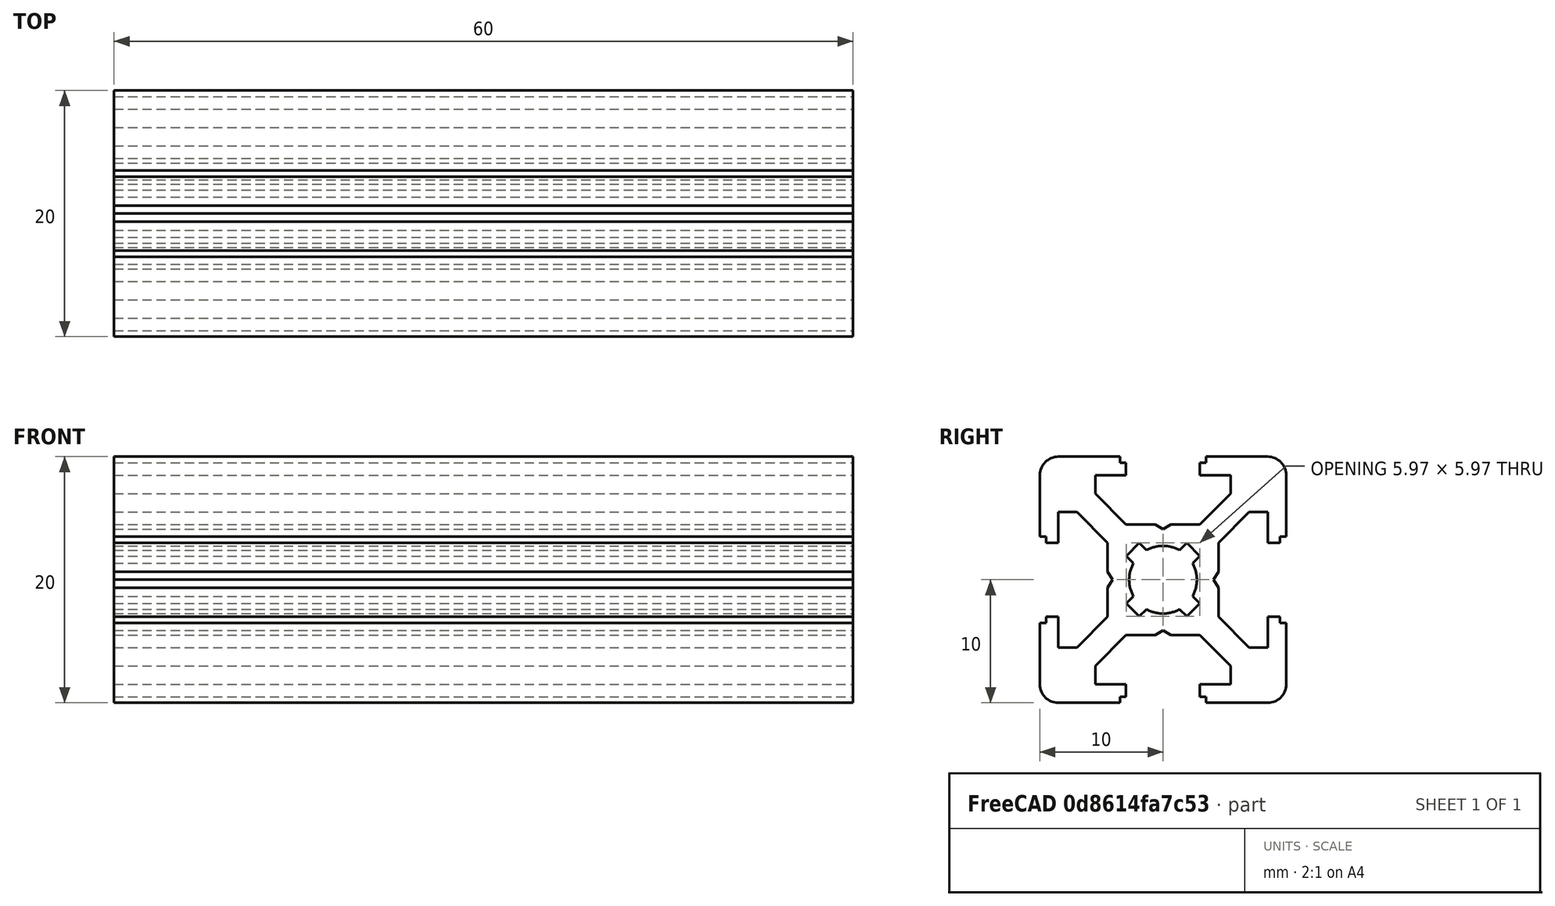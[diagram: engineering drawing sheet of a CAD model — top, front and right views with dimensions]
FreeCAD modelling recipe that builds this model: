
FCSTD DOCUMENT  (FreeCAD 0.19R)
Label: Tslot6
License: All rights reserved
LicenseURL: http://en.wikipedia.org/wiki/All_rights_reserved
objects: Sketcher::SketchObject×1, PartDesign::Pad×1, PartDesign::Body×1
note: 4 computed .brp shape members not serialized (recipe doc carries the construction recipe); baked Part::Feature solids carry a one-line shape summary decoded from their .brp

FEATURE [Sketcher::SketchObject] Sketch  label="T-Slot-Skizze"
  FullyConstrained = true
  MapMode = 5
  Placement = pos=(0,0,0) rot=(0.57735,0.57735,0.57735;2.0944rad)
  Support = -> [YZ_Plane]
  sketch-geometry (98):
    g0: LineSegment StartX=0 StartY=4.1 StartZ=0 EndX=0.65 EndY=4.5 EndZ=0
    g1: LineSegment StartX=0.65 StartY=4.5 StartZ=0 EndX=3 EndY=4.5 EndZ=0
    g2: LineSegment StartX=3 StartY=4.5 StartZ=0 EndX=5.5 EndY=7 EndZ=0
    g3: LineSegment StartX=5.5 StartY=7 StartZ=0 EndX=5.5 EndY=8.5 EndZ=0
    g4: LineSegment StartX=5.5 StartY=8.5 StartZ=0 EndX=3 EndY=8.5 EndZ=0
    g5: LineSegment StartX=3 StartY=8.5 StartZ=0 EndX=3 EndY=9.5 EndZ=0
    g6: LineSegment StartX=3 StartY=9.5 StartZ=0 EndX=3.5 EndY=9.5 EndZ=0
    g7: LineSegment StartX=3.5 StartY=9.5 StartZ=0 EndX=3.5 EndY=10 EndZ=0
    g8: LineSegment StartX=3.5 StartY=10 StartZ=0 EndX=8.5 EndY=10 EndZ=0
    g9: LineSegment StartX=10 StartY=8.5 StartZ=0 EndX=10 EndY=3.5 EndZ=0
    g10: LineSegment StartX=10 StartY=3.5 StartZ=0 EndX=9.5 EndY=3.5 EndZ=0
    g11: LineSegment StartX=9.5 StartY=3.5 StartZ=0 EndX=9.5 EndY=3 EndZ=0
    g12: LineSegment StartX=9.5 StartY=3 StartZ=0 EndX=8.5 EndY=3 EndZ=0
    g13: LineSegment StartX=8.5 StartY=3 StartZ=0 EndX=8.5 EndY=5.5 EndZ=0
    g14: LineSegment StartX=8.5 StartY=5.5 StartZ=0 EndX=7 EndY=5.5 EndZ=0
    g15: LineSegment StartX=7 StartY=5.5 StartZ=0 EndX=4.5 EndY=3 EndZ=0
    g16: LineSegment StartX=4.5 StartY=3 StartZ=0 EndX=4.5 EndY=0.65 EndZ=0
    g17: LineSegment StartX=4.5 StartY=0.65 StartZ=0 EndX=4.1 EndY=0 EndZ=0
    g18: ArcOfCircle CenterX=8.5 CenterY=8.5 CenterZ=0 NormalX=0 NormalY=0 NormalZ=1 AngleXU=0 Radius=1.5 StartAngle=0 EndAngle=1.5708
    g19: LineSegment StartX=0 StartY=-4.1 StartZ=0 EndX=0.65 EndY=-4.5 EndZ=0
    g20: LineSegment StartX=0.65 StartY=-4.5 StartZ=0 EndX=3 EndY=-4.5 EndZ=0
    g21: LineSegment StartX=3 StartY=-4.5 StartZ=0 EndX=5.5 EndY=-7 EndZ=0
    g22: LineSegment StartX=5.5 StartY=-7 StartZ=0 EndX=5.5 EndY=-8.5 EndZ=0
    g23: LineSegment StartX=5.5 StartY=-8.5 StartZ=0 EndX=3 EndY=-8.5 EndZ=0
    g24: LineSegment StartX=3 StartY=-8.5 StartZ=0 EndX=3 EndY=-9.5 EndZ=0
    g25: LineSegment StartX=3 StartY=-9.5 StartZ=0 EndX=3.5 EndY=-9.5 EndZ=0
    g26: LineSegment StartX=3.5 StartY=-9.5 StartZ=0 EndX=3.5 EndY=-10 EndZ=0
    g27: LineSegment StartX=3.5 StartY=-10 StartZ=0 EndX=8.5 EndY=-10 EndZ=0
    g28: LineSegment StartX=10 StartY=-8.5 StartZ=0 EndX=10 EndY=-3.5 EndZ=0
    g29: LineSegment StartX=10 StartY=-3.5 StartZ=0 EndX=9.5 EndY=-3.5 EndZ=0
    g30: LineSegment StartX=9.5 StartY=-3.5 StartZ=0 EndX=9.5 EndY=-3 EndZ=0
    g31: LineSegment StartX=9.5 StartY=-3 StartZ=0 EndX=8.5 EndY=-3 EndZ=0
    g32: LineSegment StartX=8.5 StartY=-3 StartZ=0 EndX=8.5 EndY=-5.5 EndZ=0
    g33: LineSegment StartX=8.5 StartY=-5.5 StartZ=0 EndX=7 EndY=-5.5 EndZ=0
    g34: LineSegment StartX=7 StartY=-5.5 StartZ=0 EndX=4.5 EndY=-3 EndZ=0
    g35: LineSegment StartX=4.5 StartY=-3 StartZ=0 EndX=4.5 EndY=-0.65 EndZ=0
    g36: ArcOfCircle CenterX=8.5 CenterY=-8.5 CenterZ=0 NormalX=0 NormalY=0 NormalZ=1 AngleXU=0 Radius=1.5 StartAngle=4.71239 EndAngle=6.28319
    g37: LineSegment StartX=4.5 StartY=-0.65 StartZ=0 EndX=4.1 EndY=0 EndZ=0
    g38: LineSegment StartX=0 StartY=-4.1 StartZ=0 EndX=-0.65 EndY=-4.5 EndZ=0
    g39: LineSegment StartX=-0.65 StartY=-4.5 StartZ=0 EndX=-3 EndY=-4.5 EndZ=0
    g40: LineSegment StartX=-3 StartY=-4.5 StartZ=0 EndX=-5.5 EndY=-7 EndZ=0
    g41: LineSegment StartX=-5.5 StartY=-7 StartZ=0 EndX=-5.5 EndY=-8.5 EndZ=0
    g42: LineSegment StartX=-5.5 StartY=-8.5 StartZ=0 EndX=-3 EndY=-8.5 EndZ=0
    g43: LineSegment StartX=-3 StartY=-8.5 StartZ=0 EndX=-3 EndY=-9.5 EndZ=0
    g44: LineSegment StartX=-3 StartY=-9.5 StartZ=0 EndX=-3.5 EndY=-9.5 EndZ=0
    g45: LineSegment StartX=-3.5 StartY=-9.5 StartZ=0 EndX=-3.5 EndY=-10 EndZ=0
    g46: LineSegment StartX=-3.5 StartY=-10 StartZ=0 EndX=-8.5 EndY=-10 EndZ=0
    g47: LineSegment StartX=-10 StartY=-8.5 StartZ=0 EndX=-10 EndY=-3.5 EndZ=0
    g48: LineSegment StartX=-10 StartY=-3.5 StartZ=0 EndX=-9.5 EndY=-3.5 EndZ=0
    g49: LineSegment StartX=-9.5 StartY=-3.5 StartZ=0 EndX=-9.5 EndY=-3 EndZ=0
    g50: LineSegment StartX=-9.5 StartY=-3 StartZ=0 EndX=-8.5 EndY=-3 EndZ=0
    g51: LineSegment StartX=-8.5 StartY=-3 StartZ=0 EndX=-8.5 EndY=-5.5 EndZ=0
    g52: LineSegment StartX=-8.5 StartY=-5.5 StartZ=0 EndX=-7 EndY=-5.5 EndZ=0
    g53: LineSegment StartX=-7 StartY=-5.5 StartZ=0 EndX=-4.5 EndY=-3 EndZ=0
    g54: LineSegment StartX=-4.5 StartY=-3 StartZ=0 EndX=-4.5 EndY=-0.65 EndZ=0
    g55: ArcOfCircle CenterX=-8.5 CenterY=-8.5 CenterZ=0 NormalX=0 NormalY=0 NormalZ=1 AngleXU=0 Radius=1.5 StartAngle=3.14159 EndAngle=4.71239
    g56: LineSegment StartX=-4.5 StartY=-0.65 StartZ=0 EndX=-4.1 EndY=0 EndZ=0
    g57: LineSegment StartX=-0.65 StartY=4.5 StartZ=0 EndX=-3 EndY=4.5 EndZ=0
    g58: LineSegment StartX=-3 StartY=4.5 StartZ=0 EndX=-5.5 EndY=7 EndZ=0
    g59: LineSegment StartX=-5.5 StartY=7 StartZ=0 EndX=-5.5 EndY=8.5 EndZ=0
    g60: LineSegment StartX=-5.5 StartY=8.5 StartZ=0 EndX=-3 EndY=8.5 EndZ=0
    g61: LineSegment StartX=-3 StartY=8.5 StartZ=0 EndX=-3 EndY=9.5 EndZ=0
    g62: LineSegment StartX=-3 StartY=9.5 StartZ=0 EndX=-3.5 EndY=9.5 EndZ=0
    g63: LineSegment StartX=-3.5 StartY=9.5 StartZ=0 EndX=-3.5 EndY=10 EndZ=0
    g64: LineSegment StartX=-3.5 StartY=10 StartZ=0 EndX=-8.5 EndY=10 EndZ=0
    g65: LineSegment StartX=-10 StartY=8.5 StartZ=0 EndX=-10 EndY=3.5 EndZ=0
    g66: LineSegment StartX=-10 StartY=3.5 StartZ=0 EndX=-9.5 EndY=3.5 EndZ=0
    g67: LineSegment StartX=-9.5 StartY=3.5 StartZ=0 EndX=-9.5 EndY=3 EndZ=0
    g68: LineSegment StartX=-9.5 StartY=3 StartZ=0 EndX=-8.5 EndY=3 EndZ=0
    g69: LineSegment StartX=-8.5 StartY=3 StartZ=0 EndX=-8.5 EndY=5.5 EndZ=0
    g70: LineSegment StartX=-8.5 StartY=5.5 StartZ=0 EndX=-7 EndY=5.5 EndZ=0
    g71: LineSegment StartX=-7 StartY=5.5 StartZ=0 EndX=-4.5 EndY=3 EndZ=0
    g72: LineSegment StartX=-4.5 StartY=3 StartZ=0 EndX=-4.5 EndY=0.65 EndZ=0
    g73: ArcOfCircle CenterX=-8.5 CenterY=8.5 CenterZ=0 NormalX=0 NormalY=0 NormalZ=1 AngleXU=0 Radius=1.5 StartAngle=1.5708 EndAngle=3.14159
    g74: LineSegment StartX=-4.5 StartY=0.65 StartZ=0 EndX=-4.1 EndY=0 EndZ=0
    g75: LineSegment StartX=0 StartY=4.1 StartZ=0 EndX=-0.65 EndY=4.5 EndZ=0
    g76: Circle CenterX=0 CenterY=0 CenterZ=0 NormalX=0 NormalY=0 NormalZ=1 AngleXU=0 Radius=3.55
    g77: Circle CenterX=0 CenterY=0 CenterZ=0 NormalX=0 NormalY=0 NormalZ=1 AngleXU=0 Radius=2.75
    g78: LineSegment StartX=1.3405 StartY=2.40116 StartZ=0 EndX=1.92324 EndY=2.9839 EndZ=0
    g79: LineSegment StartX=1.92324 StartY=2.9839 StartZ=0 EndX=2.9839 EndY=1.92324 EndZ=0
    g80: LineSegment StartX=2.9839 StartY=1.92324 StartZ=0 EndX=2.40116 EndY=1.3405 EndZ=0
    g81: ArcOfCircle CenterX=0 CenterY=0 CenterZ=0 NormalX=0 NormalY=0 NormalZ=1 AngleXU=0 Radius=2.75 StartAngle=0 EndAngle=0.509172
    g82: ArcOfCircle CenterX=0 CenterY=0 CenterZ=0 NormalX=0 NormalY=0 NormalZ=1 AngleXU=0 Radius=2.75 StartAngle=1.06162 EndAngle=1.5708
    g83: LineSegment StartX=-1.3405 StartY=2.40116 StartZ=0 EndX=-1.92324 EndY=2.9839 EndZ=0
    g84: LineSegment StartX=-1.92324 StartY=2.9839 StartZ=0 EndX=-2.9839 EndY=1.92324 EndZ=0
    g85: LineSegment StartX=-2.9839 StartY=1.92324 StartZ=0 EndX=-2.40116 EndY=1.3405 EndZ=0
    g86: ArcOfCircle CenterX=-1.3e-15 CenterY=6e-16 CenterZ=0 NormalX=0 NormalY=0 NormalZ=1 AngleXU=0 Radius=2.75 StartAngle=2.63242 EndAngle=3.14159
    g87: ArcOfCircle CenterX=-1.3e-15 CenterY=6e-16 CenterZ=0 NormalX=0 NormalY=0 NormalZ=1 AngleXU=0 Radius=2.75 StartAngle=1.5708 EndAngle=2.07997
    g88: LineSegment StartX=-1.34051 StartY=-2.40115 StartZ=0 EndX=-1.92325 EndY=-2.98389 EndZ=0
    g89: LineSegment StartX=-1.92325 StartY=-2.98389 StartZ=0 EndX=-2.9839 EndY=-1.92323 EndZ=0
    g90: LineSegment StartX=-2.9839 StartY=-1.92323 StartZ=0 EndX=-2.40116 EndY=-1.34049 EndZ=0
    g91: ArcOfCircle CenterX=-3e-16 CenterY=2e-16 CenterZ=0 NormalX=0 NormalY=0 NormalZ=1 AngleXU=0 Radius=2.75 StartAngle=3.14159 EndAngle=3.65076
    g92: ArcOfCircle CenterX=-3e-16 CenterY=2e-16 CenterZ=0 NormalX=0 NormalY=0 NormalZ=1 AngleXU=0 Radius=2.75 StartAngle=4.20321 EndAngle=4.71239
    g93: LineSegment StartX=1.34051 StartY=-2.40115 StartZ=0 EndX=1.92325 EndY=-2.98389 EndZ=0
    g94: LineSegment StartX=1.92325 StartY=-2.98389 StartZ=0 EndX=2.9839 EndY=-1.92323 EndZ=0
    g95: LineSegment StartX=2.9839 StartY=-1.92323 StartZ=0 EndX=2.40116 EndY=-1.34049 EndZ=0
    g96: ArcOfCircle CenterX=3e-16 CenterY=2e-16 CenterZ=0 NormalX=0 NormalY=0 NormalZ=1 AngleXU=0 Radius=2.75 StartAngle=4.71239 EndAngle=5.22156
    g97: ArcOfCircle CenterX=3e-16 CenterY=2e-16 CenterZ=0 NormalX=0 NormalY=0 NormalZ=1 AngleXU=0 Radius=2.75 StartAngle=5.77402 EndAngle=6.28319
  constraints (291):
    c: PointOnObject(g0,g-2)
    c: Coincident(g0,g1)
    c: Horizontal(g1)
    c: Coincident(g1,g2)
    c: Coincident(g2,g3)
    c: Vertical(g3)
    c: Coincident(g3,g4)
    c: Horizontal(g4)
    c: Coincident(g4,g5)
    c: Vertical(g5)
    c: Coincident(g5,g6)
    c: Horizontal(g6)
    c: Coincident(g6,g7)
    c: Coincident(g7,g8)
    c: Horizontal(g8)
    c: Vertical(g7)
    c: DistanceX(g-1,g5) = 3
    c: DistanceY(g4,g7) = 1.5
    c: DistanceY(g0,g7) = 5.5
    c: DistanceY(g3,g3) = 1.5
    c: DistanceY(g4,g5) = 1
    c: DistanceX(g-1,g1) = 3
    c: DistanceX(g-1,g7) = 3.5
    c: DistanceX(g0,g0) = 0.65
    c: DistanceY(g0,g0) = 0.4
    c: DistanceX(g-1,g3) = 5.5
    c: Vertical(g9)
    c: Coincident(g9,g10)
    c: Coincident(g10,g11)
    c: Coincident(g11,g12)
    c: Coincident(g12,g13)
    c: Vertical(g13)
    c: Coincident(g13,g14)
    c: Horizontal(g14)
    c: Coincident(g14,g15)
    c: Coincident(g15,g16)
    c: Vertical(g16)
    c: Coincident(g16,g17)
    c: PointOnObject(g17,g-1)
    c: Horizontal(g10)
    c: Horizontal(g12)
    c: Vertical(g11)
    c: Equal(g17,g0)
    c: Equal(g1,g16)
    c: Equal(g15,g2)
    c: Equal(g3,g14)
    c: Equal(g13,g4)
    c: Equal(g12,g5)
    c: Parallel(g15,g2)
    c: Equal(g11,g6)
    c: Equal(g10,g7)
    c: Equal(g9,g8)
    c: Tangent(g8,g18) = 1.5708
    c: Tangent(g9,g18) = 1.5708
    c: Radius(g18) = 1.5
    c: DistanceY(g-1,g8) = 10
    c: DistanceX(g-1,g9) = 10
    c: Coincident(g19,g20)
    c: Horizontal(g20)
    c: Coincident(g20,g21)
    c: Coincident(g21,g22)
    c: Vertical(g22)
    c: Coincident(g22,g23)
    c: Horizontal(g23)
    c: Coincident(g23,g24)
    c: Vertical(g24)
    c: Coincident(g24,g25)
    c: Horizontal(g25)
    c: Coincident(g25,g26)
    c: Coincident(g26,g27)
    c: Horizontal(g27)
    c: Vertical(g26)
    c: Vertical(g28)
    c: Coincident(g28,g29)
    c: Coincident(g29,g30)
    c: Coincident(g30,g31)
    c: Coincident(g31,g32)
    c: Vertical(g32)
    c: Coincident(g32,g33)
    c: Horizontal(g33)
    c: Coincident(g33,g34)
    c: Coincident(g34,g35)
    c: Vertical(g35)
    c: Coincident(g35,g37)
    c: Horizontal(g29)
    c: Horizontal(g31)
    c: Vertical(g30)
    c: Equal(g37,g19)
    c: Equal(g20,g35)
    c: Equal(g34,g21)
    c: Equal(g22,g33)
    c: Equal(g32,g23)
    c: Equal(g31,g24)
    c: Parallel(g34,g21)
    c: Equal(g30,g25)
    c: Equal(g29,g26)
    c: Equal(g28,g27)
    c: Tangent(g27,g36) = -1.5708
    c: Tangent(g28,g36) = -1.5708
    c: Radius(g36) = 1.5
    c: Equal(g9,g28)
    c: Equal(g12,g31)
    c: DistanceX(g-1,g28) = 10
    c: DistanceY(g27,g-1) = 10
    c: DistanceY(g30,g-1) = 3
    c: Equal(g33,g14)
    c: Equal(g35,g16)
    c: Equal(g17,g37)
    c: Coincident(g37,g17)
    c: Equal(g15,g34)
    c: PointOnObject(g19,g-2)
    c: DistanceY(g34,g-1) = 3
    c: DistanceX(g-1,g20) = 3
    c: Coincident(g38,g39)
    c: Horizontal(g39)
    c: Coincident(g39,g40)
    c: Coincident(g40,g41)
    c: Vertical(g41)
    c: Coincident(g41,g42)
    c: Horizontal(g42)
    c: Coincident(g42,g43)
    c: Vertical(g43)
    c: Coincident(g43,g44)
    c: Horizontal(g44)
    c: Coincident(g44,g45)
    c: Coincident(g45,g46)
    c: Horizontal(g46)
    c: Vertical(g45)
    c: Vertical(g47)
    c: Coincident(g47,g48)
    c: Coincident(g48,g49)
    c: Coincident(g49,g50)
    c: Coincident(g50,g51)
    c: Vertical(g51)
    c: Coincident(g51,g52)
    c: Horizontal(g52)
    c: Coincident(g52,g53)
    c: Coincident(g53,g54)
    c: Vertical(g54)
    c: Coincident(g54,g56)
    c: Horizontal(g48)
    c: Horizontal(g50)
    c: Vertical(g49)
    c: Equal(g39,g54)
    c: Equal(g53,g40)
    c: Equal(g41,g52)
    c: Equal(g51,g42)
    c: Equal(g50,g43)
    c: Parallel(g53,g40)
    c: Equal(g49,g44)
    c: Equal(g48,g45)
    c: Equal(g47,g46)
    c: Tangent(g46,g55) = 1.5708
    c: Tangent(g47,g55) = 1.5708
    c: Radius(g55) = 1.5
    c: Coincident(g38,g19)
    c: DistanceX(g39,g-1) = 3
    c: DistanceX(g38,g19) = 0.65
    c: DistanceY(g38,g19) = 0.4
    c: PointOnObject(g56,g-1)
    c: Equal(g56,g38)
    c: DistanceY(g53,g-1) = 3
    c: Equal(g22,g41)
    c: Equal(g42,g23)
    c: Equal(g24,g43)
    c: Equal(g25,g44)
    c: Equal(g26,g45)
    c: DistanceY(g46,g-1) = 10
    c: DistanceX(g47,g-1) = 10
    c: Coincident(g75,g57)
    c: Horizontal(g57)
    c: Coincident(g57,g58)
    c: Coincident(g58,g59)
    c: Vertical(g59)
    c: Coincident(g59,g60)
    c: Horizontal(g60)
    c: Coincident(g60,g61)
    c: Vertical(g61)
    c: Coincident(g61,g62)
    c: Horizontal(g62)
    c: Coincident(g62,g63)
    c: Coincident(g63,g64)
    c: Horizontal(g64)
    c: Vertical(g63)
    c: Vertical(g65)
    c: Coincident(g65,g66)
    c: Coincident(g66,g67)
    c: Coincident(g67,g68)
    c: Coincident(g68,g69)
    c: Vertical(g69)
    c: Coincident(g69,g70)
    c: Horizontal(g70)
    c: Coincident(g70,g71)
    c: Coincident(g71,g72)
    c: Vertical(g72)
    c: Coincident(g72,g74)
    c: Horizontal(g66)
    c: Horizontal(g68)
    c: Vertical(g67)
    c: Equal(g57,g72)
    c: Equal(g71,g58)
    c: Equal(g59,g70)
    c: Equal(g69,g60)
    c: Equal(g68,g61)
    c: Parallel(g71,g58)
    c: Equal(g67,g62)
    c: Equal(g66,g63)
    c: Equal(g65,g64)
    c: Tangent(g64,g73) = -1.5708
    c: Tangent(g65,g73) = -1.5708
    c: Radius(g73) = 1.5
    c: Equal(g74,g75)
    c: Coincident(g56,g74)
    c: Coincident(g0,g75)
    c: Equal(g0,g75)
    c: Equal(g1,g57)
    c: Equal(g2,g58)
    c: Equal(g3,g59)
    c: Equal(g4,g60)
    c: Equal(g5,g61)
    c: Equal(g6,g62)
    c: Equal(g7,g63)
    c: Equal(g8,g64)
    c: DistanceX(g65,g-1) = 10
    c: Coincident(g76,g-1)
    c: Coincident(g77,g-1)
    c: Radius(g76) = 3.55
    c: Radius(g77) = 2.75
    c: PointOnObject(g78,g77)
    c: PointOnObject(g78,g76)
    c: Coincident(g78,g79)
    c: PointOnObject(g79,g76)
    c: Coincident(g79,g80)
    c: PointOnObject(g80,g77)
    c: Coincident(g81,g-1)
    c: Coincident(g81,g80)
    c: Coincident(g82,g81)
    c: Coincident(g82,g78)
    c: Parallel(g78,g80)
    c: Parallel(g78,g2)
    c: Distance(g79) = 1.5
    c: Distance(g78,g80) = 1.5
    c: PointOnObject(g82,g-2)
    c: PointOnObject(g81,g-1)
    c: Coincident(g83,g84)
    c: Coincident(g84,g85)
    c: Coincident(g86,g85)
    c: Coincident(g87,g86)
    c: Coincident(g87,g83)
    c: Parallel(g83,g85)
    c: Distance(g84) = 1.5
    c: Distance(g83,g85) = 1.5
    c: Coincident(g82,g87)
    c: PointOnObject(g86,g-1)
    c: PointOnObject(g83,g76)
    c: PointOnObject(g83,g77)
    c: PointOnObject(g85,g77)
    c: PointOnObject(g84,g76)
    c: PointOnObject(g86,g77)
    c: Parallel(g85,g71)
    c: Coincident(g88,g89)
    c: Coincident(g89,g90)
    c: Coincident(g91,g90)
    c: Coincident(g92,g91)
    c: Coincident(g92,g88)
    c: Parallel(g88,g90)
    c: Distance(g89) = 1.5
    c: Distance(g88,g90) = 1.5
    c: PointOnObject(g88,g77)
    c: PointOnObject(g90,g77)
    c: Coincident(g86,g91)
    c: PointOnObject(g89,g76)
    c: PointOnObject(g88,g76)
    c: PointOnObject(g92,g-2)
    c: PointOnObject(g92,g77)
    c: Parallel(g88,g40)
    c: Coincident(g93,g94)
    c: Coincident(g94,g95)
    c: Coincident(g97,g95)
    c: Coincident(g96,g97)
    c: Coincident(g96,g93)
    c: Parallel(g93,g95)
    c: Distance(g94) = 1.5
    c: Distance(g93,g95) = 1.5
    c: Coincident(g81,g97)
    c: Coincident(g92,g96)
    c: PointOnObject(g93,g77)
    c: PointOnObject(g95,g77)
    c: PointOnObject(g94,g76)
    c: PointOnObject(g93,g76)
    c: Parallel(g93,g21)
FEATURE [PartDesign::Pad] Pad  label="T-Slot-Element"
  Direction = (1,1,1)
  Length = 60
  Length2 = 100
  Placement = pos=(0,0,0) rot=(0.57735,0.57735,0.57735;2.0944rad)
  Profile = -> Sketch
  Type = 0
FEATURE [PartDesign::Body] Body  label="T-Slot-Profil 20x20"
  Group = -> [Sketch,Pad]
  Origin = -> Origin
  Tip = -> Pad
